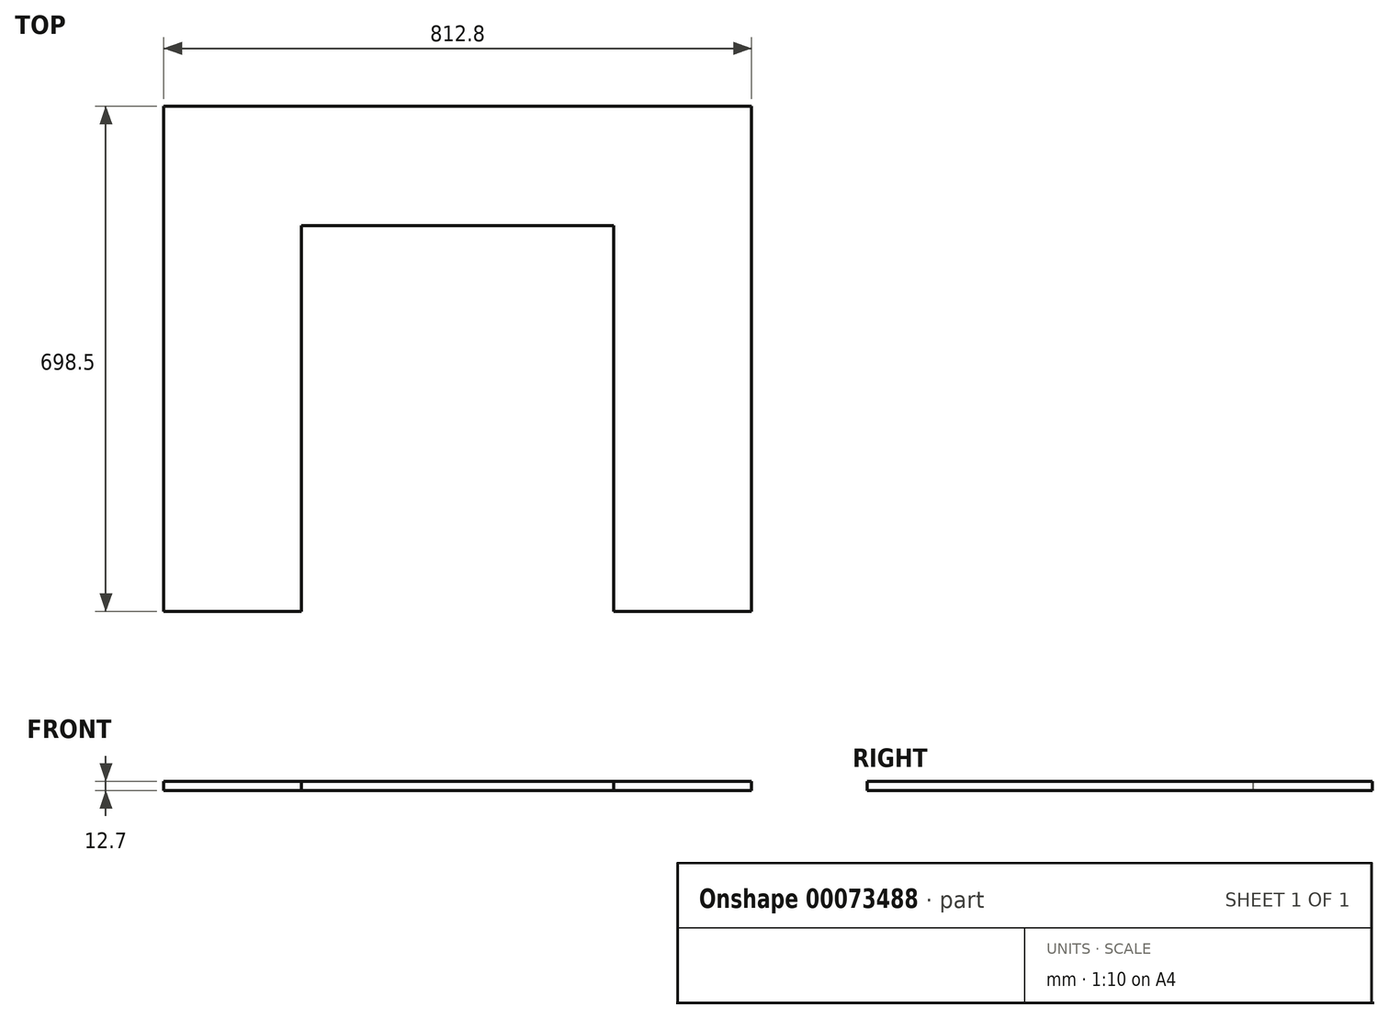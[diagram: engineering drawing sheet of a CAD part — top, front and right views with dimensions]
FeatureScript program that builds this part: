
annotation { "Feature Type Name" : "Feature", "Feature Type Description" : "" }
export const myFeature = defineFeature(function(context is Context, id is Id, definition is map)
    precondition{}
    {
        {
            var Q0;
            Q0=qCreatedBy(makeId("Top.planeOp"),FACE);
            var sketch = newSketch(context, id + "F0", { "sketchPlane" : qUnion([Q0])});
            skLineSegment(sketch, "E0.bottom", {"start": v(-317.7, -368.44) * mm, "end": v(495.1, -368.44) * mm});
            skLineSegment(sketch, "E0.top", {"start": v(-317.7, 330.06) * mm, "end": v(495.1, 330.06) * mm});
            skLineSegment(sketch, "E0.left", {"start": v(-317.7, -368.44) * mm, "end": v(-317.7, 330.06) * mm});
            skLineSegment(sketch, "E0.right", {"start": v(495.1, -368.44) * mm, "end": v(495.1, 330.06) * mm});
            skLineSegment(sketch, "E1", {"start": v(88.7, -368.44) * mm, "end": v(88.7, 612.74) * mm, "construction": true});
            skPoint(sketch, "E1.endSnap0", {"position": v(88.7, 330.06) * mm});
            skLineSegment(sketch, "E2", {"start": v(-376.62, 164.96) * mm, "end": v(348.78, 164.96) * mm, "construction": true});
            skLineSegment(sketch, "E3.bottom", {"start": v(-127.2, 164.96) * mm, "end": v(304.6, 164.96) * mm});
            skLineSegment(sketch, "E3.top", {"start": v(-127.2, -397.31) * mm, "end": v(304.6, -397.31) * mm});
            skLineSegment(sketch, "E3.left", {"start": v(-127.2, 164.96) * mm, "end": v(-127.2, -397.31) * mm});
            skLineSegment(sketch, "E3.right", {"start": v(304.6, 164.96) * mm, "end": v(304.6, -397.31) * mm});
            skSolve(sketch);
        }
        {
            var Q0;
            Q0=makeQuery(id+"F0.imprint","IMPRINT",FACE,{"disambiguationData":[TD([[makeQuery(id+"F0.imprint","IMPRINT",EDGE,{"derivedFrom":sQuery(id+"F0.wireOp",EDGE,"E0.bottom")}),1.0]])]});
            extrude(context, id + "F1", {"entities" : qUnion([Q0]), "depth" : 12.7 * mm});
        }
    });
